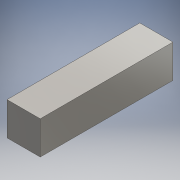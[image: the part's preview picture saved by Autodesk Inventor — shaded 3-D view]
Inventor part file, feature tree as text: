
AUTODESK INVENTOR PART (.ipt)
format: ipt  version: 2016 (Build 200138000, 138)  size: 88,576 bytes
history: native  units: mm
features: extrude x1, sketch x1
ambient origin geometry x8: Origin, YZ Plane, XZ Plane, XY Plane, X Axis, Y Axis, Z Axis, Center Point
bodies: Solid1 (feature_tree)
feature tree (2):
  extrude  "Extrusion1"  Depth=200.0mm
  sketch  "Sketch1"  dims[d0=800.0mm d1=200.0mm d2=200.0mm d3=0.0mm]
